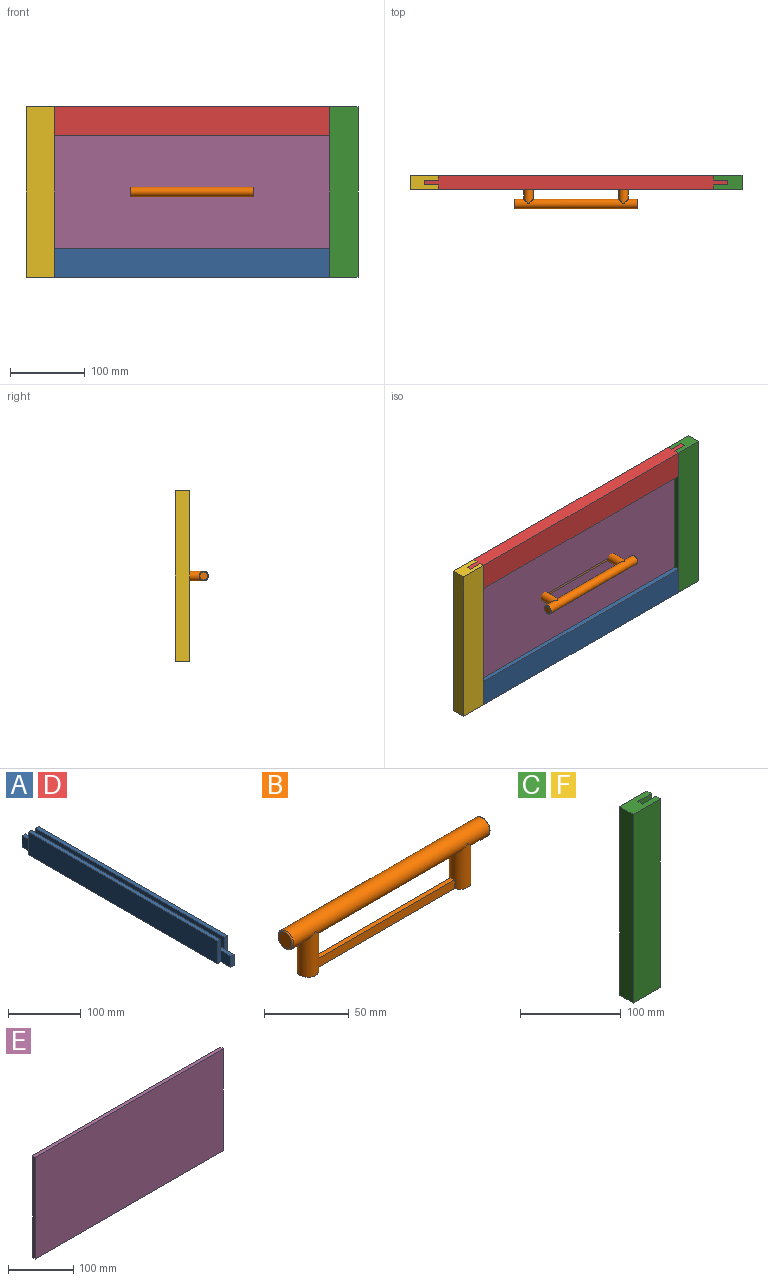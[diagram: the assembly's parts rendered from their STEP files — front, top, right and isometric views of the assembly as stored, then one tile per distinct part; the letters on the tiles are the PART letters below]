
ASSEMBLY  parts=6 mates=5
PART A: 18 faces, bbox 19.1x406.4x38.1 mm
  f0: plane 368.3x6.35mm, normal (0,0,1), area 2338.7mm2, adj f4,f6,f10,f15
  f1: plane 19.05x6.35mm, normal (0,1,0), area 121mm2, adj f8,f9,f14,f17
  f2: plane 19.05x6.35mm, normal (0,-1,0), area 121mm2, adj f8,f9,f11,f13
  f3: plane 368.3x38.1mm, normal (-1,0,0), area 14032.2mm2, adj f5,f8,f12,f16
  f4: plane 368.3x38.1mm, normal (1,0,0), area 14032.2mm2, adj f0,f8,f10,f15
  f5: plane 368.3x6.35mm, normal (0,0,1), area 2338.7mm2, adj f3,f7,f12,f16
  f6: plane 368.3x19.05mm, normal (-1,0,0), area 7016.1mm2, adj f0,f9,f10,f15
  f7: plane 368.3x19.05mm, normal (1,0,0), area 7016.1mm2, adj f5,f9,f12,f16
  f8: plane 406.4x19.05mm, normal (0,0,-1), area 7258mm2, adj f1,f2,f3,f4,f10,f11,f12,f13
  f9: plane 406.4x6.35mm, normal (0,0,1), area 2580.6mm2, adj f1,f2,f6,f7,f11,f13,f14,f17
  f10: plane 38.1x6.35mm, normal (0,-1,0), area 241.9mm2, adj f0,f4,f6,f8,f11
  f11: plane 19.05x19.05mm, normal (1,0,0), area 362.9mm2, adj f2,f8,f9,f10
  f12: plane 38.1x6.35mm, normal (0,-1,0), area 241.9mm2, adj f3,f5,f7,f8,f13
  f13: plane 19.05x19.05mm, normal (-1,0,0), area 362.9mm2, adj f2,f8,f9,f12
  f14: plane 19.05x19.05mm, normal (1,0,0), area 362.9mm2, adj f1,f8,f9,f15
  f15: plane 38.1x6.35mm, normal (0,1,0), area 241.9mm2, adj f0,f4,f6,f8,f14
  f16: plane 38.1x6.35mm, normal (0,1,0), area 241.9mm2, adj f3,f5,f7,f8,f17
  f17: plane 19.05x19.05mm, normal (-1,0,0), area 362.9mm2, adj f1,f8,f9,f16
PART B: 11 faces, bbox 165.1x13.7x38.6 mm
  f0: cylinder r=6.35mm len=31.75mm, axis (0,0,-1), area 1085.1mm2, adj f1,f2,f6,f7,f8
  f1: plane 139.7x12.7mm, normal (0,0,-1), area 616.7mm2, adj f0,f3,f6,f7
  f2: cylinder r=6.35mm len=163.51mm, axis (-1,0,0), area 6201.3mm2, adj f0,f3,f9,f10
  f3: cylinder r=6.35mm len=31.75mm, axis (0,0,-1), area 1085.1mm2, adj f1,f2,f6,f7,f8
  f4: plane 11.11x11.11mm, normal (1,0,0), area 97mm2, adj f10
  f5: plane 11.11x11.11mm, normal (-1,0,0), area 97mm2, adj f9
  f6: plane 114.7x6.35mm, normal (0,-1,0), area 728.4mm2, adj f0,f1,f3,f8
  f7: plane 114.7x6.35mm, normal (0,1,0), area 728.4mm2, adj f0,f1,f3,f8
  f8: plane 114.7x3.18mm, normal (0,0,1), area 363.3mm2, adj f0,f3,f6,f7
  f9: torus R=5.56mm, axis (1,0,0), area 47.5mm2, adj f2,f5
  f10: torus R=5.56mm, axis (1,0,0), area 47.5mm2, adj f2,f4
PART C: 10 faces, bbox 38.1x19.1x228.6 mm
  f0: plane 228.6x6.35mm, normal (1,0,0), area 1451.6mm2, adj f1,f2,f6,f7
  f1: plane 38.1x19.05mm, normal (0,0,1), area 604.8mm2, adj f0,f3,f4,f5,f6,f7,f8,f9
  f2: plane 38.1x19.05mm, normal (0,0,-1), area 604.8mm2, adj f0,f3,f4,f5,f6,f7,f8,f9
  f3: plane 228.6x19.05mm, normal (-1,0,0), area 4354.8mm2, adj f1,f2,f4,f6
  f4: plane 228.6x38.1mm, normal (0,-1,0), area 8709.7mm2, adj f1,f2,f3,f5
  f5: plane 228.6x6.35mm, normal (1,0,0), area 1451.6mm2, adj f1,f2,f4,f9
  f6: plane 228.6x38.1mm, normal (0,1,0), area 8709.7mm2, adj f0,f1,f2,f3
  f7: plane 228.6x19.05mm, normal (0,-1,0), area 4354.8mm2, adj f0,f1,f2,f8
  f8: plane 228.6x6.35mm, normal (1,0,0), area 1451.6mm2, adj f1,f2,f7,f9
  f9: plane 228.6x19.05mm, normal (0,1,0), area 4354.8mm2, adj f1,f2,f5,f8
PART D: same geometry as A
PART E: 6 faces, bbox 406.4x6.4x190.5 mm
  f0: plane 190.5x6.35mm, normal (-1,0,0), area 1209.7mm2, adj f1,f3,f4,f5
  f1: plane 406.4x6.35mm, normal (0,0,-1), area 2580.6mm2, adj f0,f2,f4,f5
  f2: plane 190.5x6.35mm, normal (1,0,0), area 1209.7mm2, adj f1,f3,f4,f5
  f3: plane 406.4x6.35mm, normal (0,0,1), area 2580.6mm2, adj f0,f2,f4,f5
  f4: plane 406.4x190.5mm, normal (0,-1,0), area 77419.2mm2, adj f0,f1,f2,f3
  f5: plane 406.4x190.5mm, normal (0,1,0), area 77419.2mm2, adj f0,f1,f2,f3
PART F: same geometry as C
PLACE A rot(axis=(0,0,-1),90deg) t=(425.45,19.05,0)mm
PLACE B rot(axis=(1,0,0),90deg) t=(222.25,12.7,114.3)mm
PLACE C rot(axis=(0,0,1),180deg) t=(444.5,19.05,0)mm
PLACE D rot(axis=(0.71,0.71,0),180deg) t=(425.45,0,228.6)mm
PLACE E t=(19.05,12.7,19.05)mm
PLACE F at identity
MATE fastened C.f8 <-> D.f1  axis (-1,0,0) through (425.45,9.53,228.6)mm
MATE fastened D.f2 <-> F.f8  axis (-1,0,0) through (19.05,9.53,228.6)mm
MATE fastened A.f2 <-> F.f8  axis (-1,0,0) through (19.05,9.53,0)mm
MATE fastened E.f3 <-> D.f9  axis (0,0,1) through (222.25,9.53,209.55)mm
MATE fastened B.f8 <-> E.f4  axis (0,-1,0) through (222.25,6.35,114.3)mm
